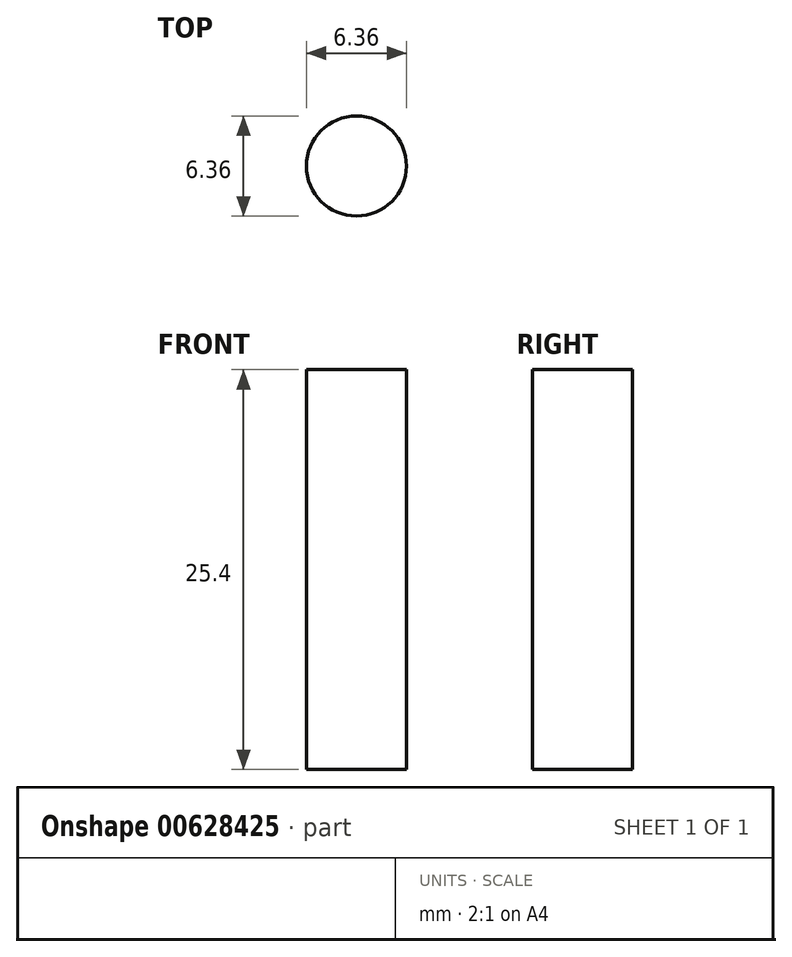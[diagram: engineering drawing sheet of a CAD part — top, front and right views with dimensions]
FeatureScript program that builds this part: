
annotation { "Feature Type Name" : "Feature", "Feature Type Description" : "" }
export const myFeature = defineFeature(function(context is Context, id is Id, definition is map)
    precondition{}
    {
        {
            var Q0;
            Q0=qCreatedBy(makeId("Top.planeOp"),FACE);
            var sketch = newSketch(context, id + "F0", { "sketchPlane" : qUnion([Q0])});
            skCircle(sketch, "E0", {"center": v(0, 0) * mm, "radius": 3.18 * mm});
            skSolve(sketch);
        }
        {
            var Q0;
            Q0=makeQuery(id+"F0.imprint","IMPRINT",FACE,{"disambiguationData":[TD([[makeQuery(id+"F0.imprint","IMPRINT",EDGE,{"derivedFrom":sQuery(id+"F0.wireOp",EDGE,"E0")}),1.0]])]});
            extrude(context, id + "F1", {"entities" : qUnion([Q0]), "depth" : 25.4 * mm, "offsetDistance" : 25.4 * mm});
        }
    });
